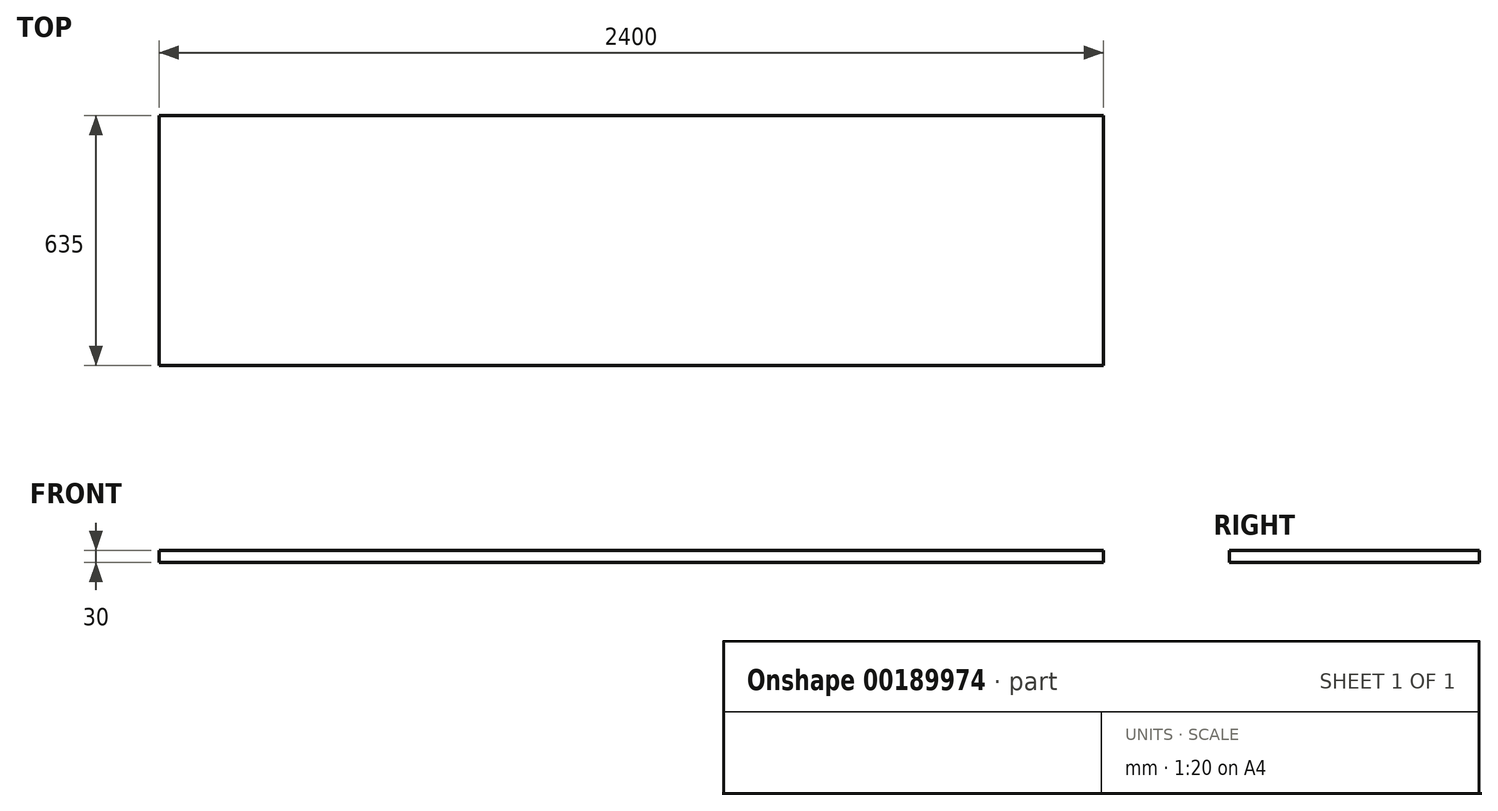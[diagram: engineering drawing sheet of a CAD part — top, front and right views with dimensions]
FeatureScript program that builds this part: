
annotation { "Feature Type Name" : "Feature", "Feature Type Description" : "" }
export const myFeature = defineFeature(function(context is Context, id is Id, definition is map)
    precondition{}
    {
        {
            var Q0;
            Q0=qCreatedBy(makeId("Top.planeOp"),FACE);
            var sketch = newSketch(context, id + "F0", { "sketchPlane" : qUnion([Q0])});
            skLineSegment(sketch, "E0.bottom", {"start": v(0, 0) * mm, "end": v(2400, 0) * mm});
            skLineSegment(sketch, "E0.top", {"start": v(0, 635) * mm, "end": v(2400, 635) * mm});
            skLineSegment(sketch, "E0.left", {"start": v(0, 0) * mm, "end": v(0, 635) * mm});
            skLineSegment(sketch, "E0.right", {"start": v(2400, 0) * mm, "end": v(2400, 635) * mm});
            skSolve(sketch);
        }
        {
            var Q0;
            Q0=makeQuery(id+"F0.imprint","IMPRINT",FACE,{"disambiguationData":[TD([[makeQuery(id+"F0.imprint","IMPRINT",EDGE,{"derivedFrom":sQuery(id+"F0.wireOp",EDGE,"E0.bottom")}),1.0]])]});
            extrude(context, id + "F1", {"entities" : qUnion([Q0]), "depth" : 30 * mm});
        }
    });
